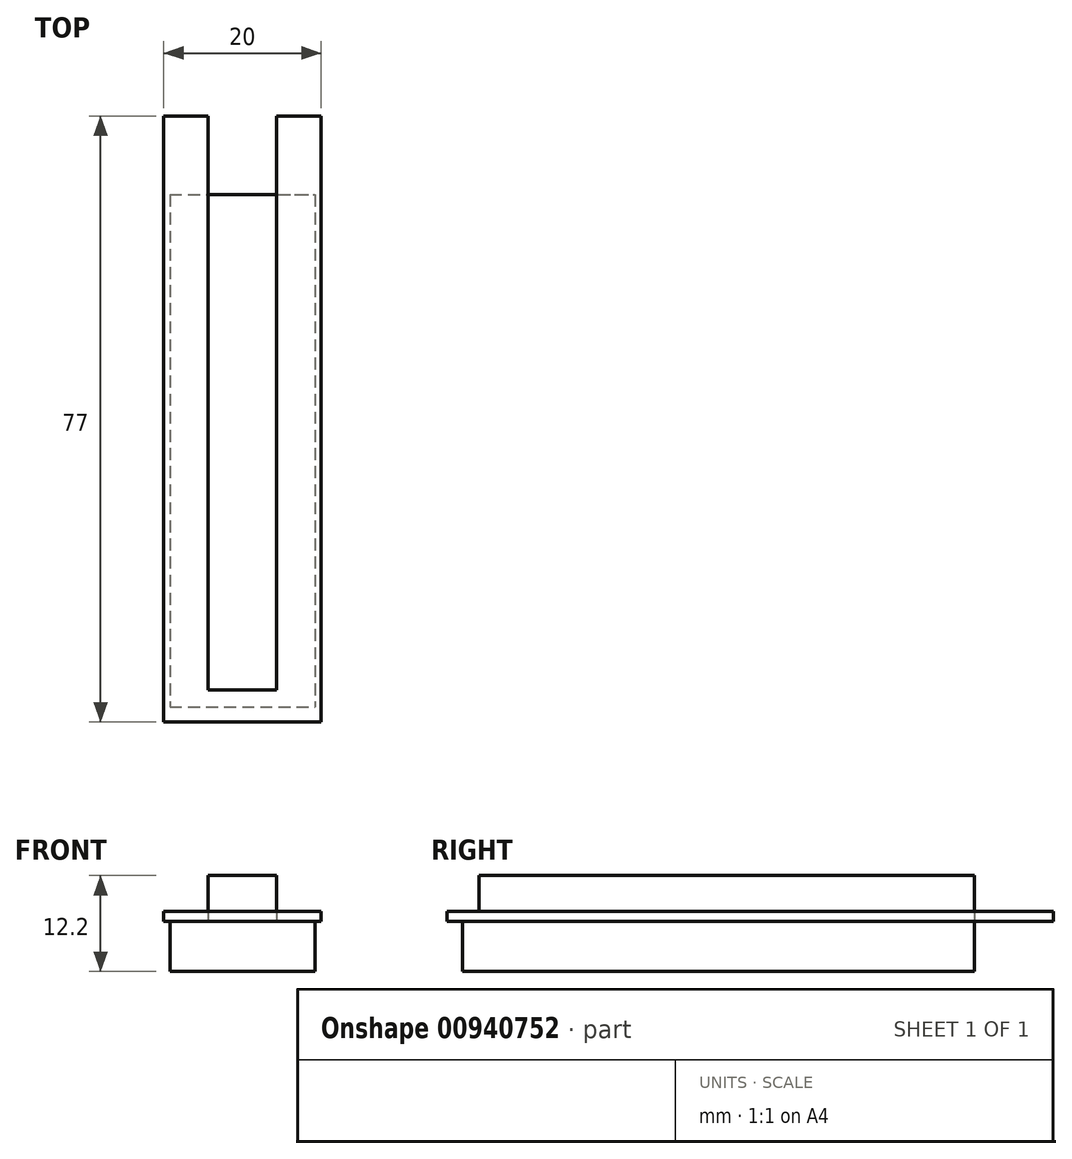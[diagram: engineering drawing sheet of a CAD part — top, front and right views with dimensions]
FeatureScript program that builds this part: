
annotation { "Feature Type Name" : "Feature", "Feature Type Description" : "" }
export const myFeature = defineFeature(function(context is Context, id is Id, definition is map)
    precondition{}
    {
        {
            var Q0;
            Q0=qCreatedBy(makeId("Top.planeOp"),FACE);
            var sketch = newSketch(context, id + "F0", { "sketchPlane" : qUnion([Q0])});
            skLineSegment(sketch, "E0.top", {"start": v(10, -38.5) * mm, "end": v(-10, -38.5) * mm});
            skLineSegment(sketch, "E0.left", {"start": v(10, 38.5) * mm, "end": v(10, -38.5) * mm});
            skLineSegment(sketch, "E0.right", {"start": v(-10, 38.5) * mm, "end": v(-10, -38.5) * mm});
            skPoint(sketch, "E0.middle", {"position": v(0, 0) * mm});
            skLineSegment(sketch, "E1", {"start": v(-10, 38.5) * mm, "end": v(-4.35, 38.5) * mm});
            skLineSegment(sketch, "E2", {"start": v(10, 38.5) * mm, "end": v(4.35, 38.5) * mm});
            skLineSegment(sketch, "E3", {"start": v(-4.35, 38.5) * mm, "end": v(-4.35, 28.5) * mm});
            skLineSegment(sketch, "E4", {"start": v(-4.35, 28.5) * mm, "end": v(4.35, 28.5) * mm});
            skLineSegment(sketch, "E5", {"start": v(4.35, 28.5) * mm, "end": v(4.35, 38.5) * mm});
            skSolve(sketch);
        }
        {
            var Q0;
            Q0=makeQuery(id+"F0.imprint","IMPRINT",FACE,{"disambiguationData":[TD([[makeQuery(id+"F0.imprint","IMPRINT",EDGE,{"derivedFrom":sQuery(id+"F0.wireOp",EDGE,"E0.top")}),-1.0]])]});
            extrude(context, id + "F1", {"entities" : qUnion([Q0]), "depth" : 1.25 * mm, "offsetDistance" : 25 * mm});
        }
        {
            var Q0;
            Q0=makeQuery(id+"F1.opExtrude","CAP_FACE",FACE,{"disambiguationData":[OSD([sQuery(id+"F0.wireOp",EDGE,"E0.top"),sQuery(id+"F0.wireOp",EDGE,"E0.left"),sQuery(id+"F0.wireOp",EDGE,"E0.right"),sQuery(id+"F0.wireOp",EDGE,"E1"),sQuery(id+"F0.wireOp",EDGE,"E2"),sQuery(id+"F0.wireOp",EDGE,"E3"),sQuery(id+"F0.wireOp",EDGE,"E4"),sQuery(id+"F0.wireOp",EDGE,"E5")])],"isStart":true});
            var sketch = newSketch(context, id + "F2", { "sketchPlane" : qUnion([Q0])});
            skLineSegment(sketch, "E6.bottom", {"start": v(-4.35, -28.5) * mm, "end": v(4.35, -28.5) * mm});
            skLineSegment(sketch, "E6.top", {"start": v(-4.35, 34.42) * mm, "end": v(4.35, 34.42) * mm});
            skLineSegment(sketch, "E6.left", {"start": v(-4.35, -28.5) * mm, "end": v(-4.35, 34.42) * mm});
            skLineSegment(sketch, "E6.right", {"start": v(4.35, -28.5) * mm, "end": v(4.35, 34.42) * mm});
            skSolve(sketch);
        }
        {
            var Q0;
            Q0 = qSketchRegion(id + "F2", true);
            extrude(context, id + "F3", {"entities" : qUnion([Q0]), "operationType" : NewBodyOperationType.ADD, "oppositeDirection" : true, "depth" : 5.8 * mm, "offsetDistance" : 25 * mm});
        }
        {
            var Q0;
            Q0=makeQuery(id+"F1.opExtrude","CAP_FACE",FACE,{"disambiguationData":[OSD([sQuery(id+"F0.wireOp",EDGE,"E0.top"),sQuery(id+"F0.wireOp",EDGE,"E0.left"),sQuery(id+"F0.wireOp",EDGE,"E0.right"),sQuery(id+"F0.wireOp",EDGE,"E1"),sQuery(id+"F0.wireOp",EDGE,"E2"),sQuery(id+"F0.wireOp",EDGE,"E3"),sQuery(id+"F0.wireOp",EDGE,"E4"),sQuery(id+"F0.wireOp",EDGE,"E5")])],"isStart":true});
            var sketch = newSketch(context, id + "F4", { "sketchPlane" : qUnion([Q0])});
            skLineSegment(sketch, "E7.bottom", {"start": v(-9.2, -28.5) * mm, "end": v(9.2, -28.5) * mm});
            skLineSegment(sketch, "E7.top", {"start": v(-9.2, 36.57) * mm, "end": v(9.2, 36.57) * mm});
            skLineSegment(sketch, "E7.left", {"start": v(-9.2, -28.5) * mm, "end": v(-9.2, 36.57) * mm});
            skLineSegment(sketch, "E7.right", {"start": v(9.2, -28.5) * mm, "end": v(9.2, 36.57) * mm});
            skLineSegment(sketch, "E8", {"start": v(9.2, -28.5) * mm, "end": v(10, -28.5) * mm});
            skLineSegment(sketch, "E9", {"start": v(-9.2, -28.5) * mm, "end": v(-10, -28.5) * mm});
            skSolve(sketch);
        }
        {
            var Q0;
            Q0=makeQuery(id+"F4.imprint","IMPRINT",FACE,{"disambiguationData":[TD([[makeQuery(id+"F4.imprint","IMPRINT",EDGE,{"derivedFrom":sQuery(id+"F4.wireOp",EDGE,"E7.top")}),-1.0]])]});
            extrude(context, id + "F5", {"entities" : qUnion([Q0]), "operationType" : NewBodyOperationType.ADD, "depth" : 6.4 * mm, "offsetDistance" : 25 * mm});
        }
    });
